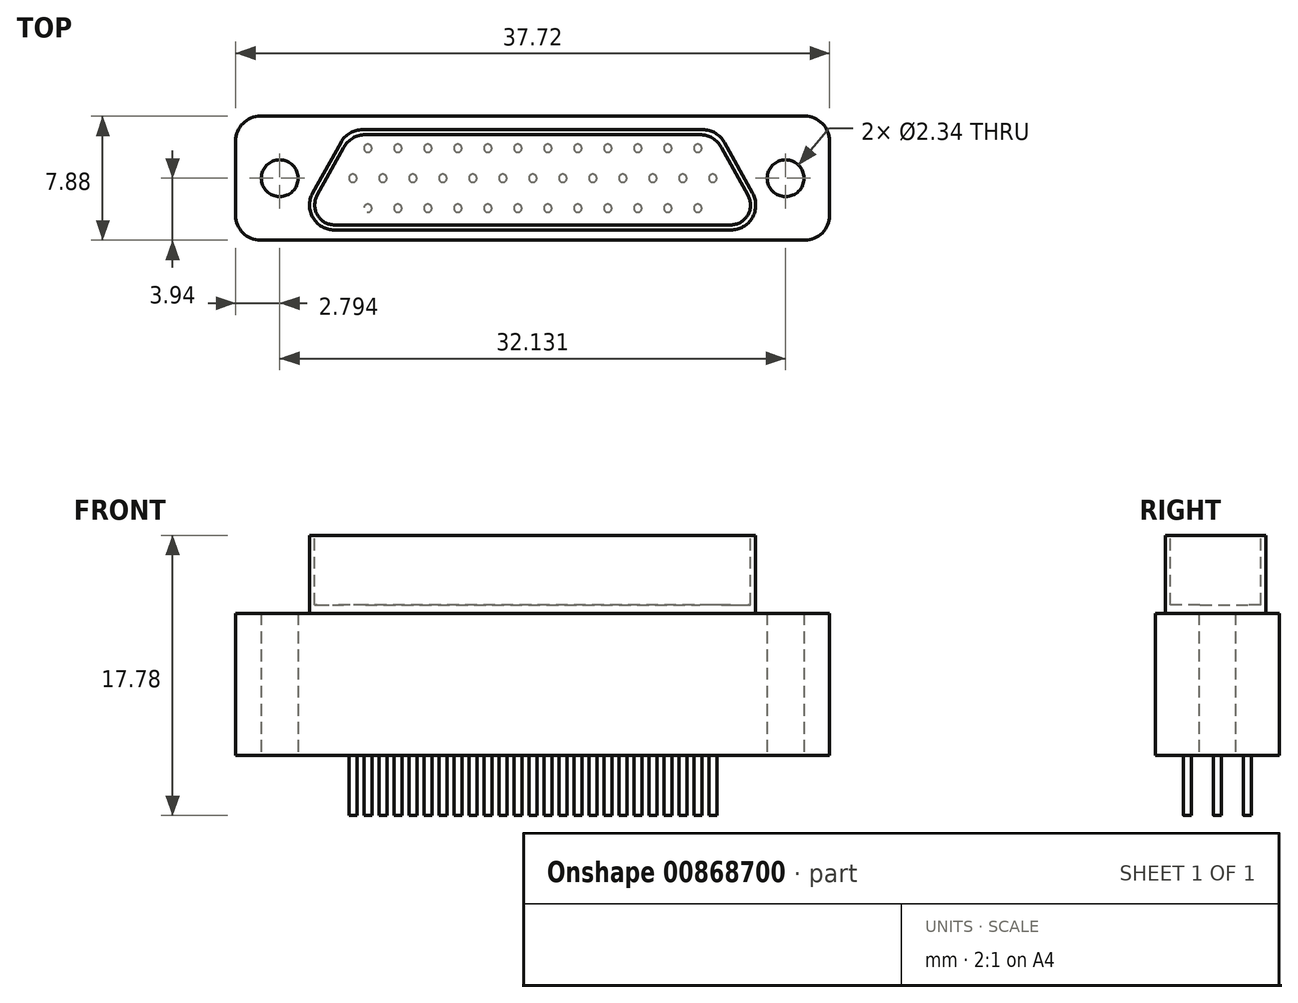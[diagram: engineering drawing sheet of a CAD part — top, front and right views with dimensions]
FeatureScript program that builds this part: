
annotation { "Feature Type Name" : "Feature", "Feature Type Description" : "" }
export const myFeature = defineFeature(function(context is Context, id is Id, definition is map)
    precondition{}
    {
        {
            var Q0;
            Q0=qCreatedBy(makeId("Top.planeOp"),FACE);
            var sketch = newSketch(context, id + "F0", { "sketchPlane" : qUnion([Q0])});
            skLineSegment(sketch, "E0.bottom", {"start": v(-17.28, 3.94) * mm, "end": v(17.28, 3.94) * mm});
            skLineSegment(sketch, "E0.top", {"start": v(-17.28, -3.94) * mm, "end": v(17.28, -3.94) * mm});
            skLineSegment(sketch, "E0.left", {"start": v(-18.86, 2.36) * mm, "end": v(-18.86, -2.36) * mm});
            skLineSegment(sketch, "E0.right", {"start": v(18.86, 2.36) * mm, "end": v(18.86, -2.36) * mm});
            skPoint(sketch, "E0.middle", {"position": v(0, 0) * mm});
            skCircle(sketch, "E1", {"center": v(-16.07, 0) * mm, "radius": 1.17 * mm});
            skCircle(sketch, "E2", {"center": v(16.07, 0) * mm, "radius": 1.17 * mm});
            skPoint(sketch, "E3.visualSharp", {"position": v(-18.86, -3.94) * mm});
            skArc(sketch, "E3.filletArc", {"start": v(-18.86, -2.36) * mm, "mid": v(-18.4, -3.48) * mm, "end": v(-17.28, -3.94) * mm});
            skPoint(sketch, "E4.visualSharp", {"position": v(-18.86, 3.94) * mm});
            skArc(sketch, "E4.filletArc", {"start": v(-17.28, 3.94) * mm, "mid": v(-18.4, 3.48) * mm, "end": v(-18.86, 2.36) * mm});
            skPoint(sketch, "E5.visualSharp", {"position": v(18.86, 3.94) * mm});
            skArc(sketch, "E5.filletArc", {"start": v(18.86, 2.36) * mm, "mid": v(18.4, 3.48) * mm, "end": v(17.28, 3.94) * mm});
            skPoint(sketch, "E6.visualSharp", {"position": v(18.86, -3.94) * mm});
            skArc(sketch, "E6.filletArc", {"start": v(17.28, -3.94) * mm, "mid": v(18.4, -3.48) * mm, "end": v(18.86, -2.36) * mm});
            skSolve(sketch);
        }
        {
            var Q0;
            Q0=makeQuery(id+"F0.imprint","IMPRINT",FACE,{"disambiguationData":[TD([[makeQuery(id+"F0.imprint","IMPRINT",EDGE,{"derivedFrom":sQuery(id+"F0.wireOp",EDGE,"E0.bottom")}),-1.0]])]});
            extrude(context, id + "F1", {"entities" : qUnion([Q0]), "endBound" : BoundingType.SYMMETRIC, "depth" : 9.02 * mm, "offsetDistance" : 25.4 * mm});
        }
        {
            var Q0;
            Q0=makeQuery(id+"F1.opExtrude","CAP_FACE",FACE,{"disambiguationData":[OSD([sQuery(id+"F0.wireOp",EDGE,"E0.bottom"),sQuery(id+"F0.wireOp",EDGE,"E0.top"),sQuery(id+"F0.wireOp",EDGE,"E0.left"),sQuery(id+"F0.wireOp",EDGE,"E0.right"),sQuery(id+"F0.wireOp",EDGE,"E1"),sQuery(id+"F0.wireOp",EDGE,"E2"),sQuery(id+"F0.wireOp",EDGE,"E3.filletArc"),sQuery(id+"F0.wireOp",EDGE,"E4.filletArc"),sQuery(id+"F0.wireOp",EDGE,"E5.filletArc"),sQuery(id+"F0.wireOp",EDGE,"E6.filletArc")])],"isStart":false});
            var sketch = newSketch(context, id + "F2", { "sketchPlane" : qUnion([Q0])});
            skPoint(sketch, "E7.middle", {"position": v(0, 0) * mm});
            skLineSegment(sketch, "E8.top", {"start": v(12.6, -3.29) * mm, "end": v(-12.6, -3.29) * mm});
            skLineSegment(sketch, "E9", {"start": v(-10.8, 3.09) * mm, "end": v(10.8, 3.09) * mm});
            skLineSegment(sketch, "E10", {"start": v(-13.97, -0.95) * mm, "end": v(-12.18, 2.27) * mm});
            skLineSegment(sketch, "E11", {"start": v(12.18, 2.27) * mm, "end": v(13.97, -0.95) * mm});
            skPoint(sketch, "E12.visualSharp", {"position": v(-11.73, 3.09) * mm});
            skArc(sketch, "E12.filletArc", {"start": v(-10.8, 3.09) * mm, "mid": v(-11.6, 2.87) * mm, "end": v(-12.18, 2.27) * mm});
            skPoint(sketch, "E13.visualSharp", {"position": v(-15.27, -3.29) * mm});
            skArc(sketch, "E13.filletArc", {"start": v(-13.97, -0.95) * mm, "mid": v(-13.95, -2.51) * mm, "end": v(-12.6, -3.29) * mm});
            skPoint(sketch, "E14.visualSharp", {"position": v(15.27, -3.29) * mm});
            skArc(sketch, "E14.filletArc", {"start": v(12.6, -3.29) * mm, "mid": v(13.95, -2.51) * mm, "end": v(13.97, -0.95) * mm});
            skPoint(sketch, "E15.visualSharp", {"position": v(11.73, 3.09) * mm});
            skArc(sketch, "E15.filletArc", {"start": v(12.18, 2.27) * mm, "mid": v(11.6, 2.87) * mm, "end": v(10.8, 3.09) * mm});
            skSolve(sketch);
        }
        {
            var Q0;
            Q0=qSketchRegion(id+"F2",true);
            extrude(context, id + "F3", {"entities" : qUnion([Q0]), "operationType" : NewBodyOperationType.ADD, "depth" : 4.95 * mm, "offsetDistance" : 25.4 * mm});
        }
        {
            var Q0;
            Q0=makeQuery(id+"F3.opExtrude","CAP_FACE",FACE,{"disambiguationData":[OSD([sQuery(id+"F2.wireOp",EDGE,"E8.top"),sQuery(id+"F2.wireOp",EDGE,"E9"),sQuery(id+"F2.wireOp",EDGE,"E10"),sQuery(id+"F2.wireOp",EDGE,"E11"),sQuery(id+"F2.wireOp",EDGE,"E12.filletArc"),sQuery(id+"F2.wireOp",EDGE,"E13.filletArc"),sQuery(id+"F2.wireOp",EDGE,"E14.filletArc"),sQuery(id+"F2.wireOp",EDGE,"E15.filletArc")])],"isStart":false});
            var sketch = newSketch(context, id + "F4", { "sketchPlane" : qUnion([Q0])});
            skLineSegment(sketch, "E16", {"start": v(-10.62, 2.77) * mm, "end": v(10.62, 2.77) * mm});
            skLineSegment(sketch, "E17", {"start": v(12, 1.96) * mm, "end": v(13.68, -1.09) * mm});
            skLineSegment(sketch, "E18", {"start": v(12.57, -2.97) * mm, "end": v(-12.57, -2.97) * mm});
            skLineSegment(sketch, "E19", {"start": v(-13.68, -1.09) * mm, "end": v(-12, 1.96) * mm});
            skPoint(sketch, "E20.visualSharp", {"position": v(-14.73, -2.97) * mm});
            skArc(sketch, "E20.filletArc", {"start": v(-13.68, -1.09) * mm, "mid": v(-13.66, -2.35) * mm, "end": v(-12.57, -2.97) * mm});
            skPoint(sketch, "E21.visualSharp", {"position": v(-11.54, 2.77) * mm});
            skArc(sketch, "E21.filletArc", {"start": v(-10.62, 2.77) * mm, "mid": v(-11.42, 2.55) * mm, "end": v(-12, 1.96) * mm});
            skPoint(sketch, "E22.visualSharp", {"position": v(11.55, 2.77) * mm});
            skArc(sketch, "E22.filletArc", {"start": v(12, 1.96) * mm, "mid": v(11.42, 2.55) * mm, "end": v(10.62, 2.77) * mm});
            skPoint(sketch, "E23.visualSharp", {"position": v(14.73, -2.97) * mm});
            skArc(sketch, "E23.filletArc", {"start": v(12.57, -2.97) * mm, "mid": v(13.67, -2.35) * mm, "end": v(13.68, -1.09) * mm});
            skSolve(sketch);
        }
        {
            var Q0;
            Q0=qSketchRegion(id+"F4",true);
            extrude(context, id + "F5", {"entities" : qUnion([Q0]), "operationType" : NewBodyOperationType.REMOVE, "depth" : -4.4 * mm, "offsetDistance" : 25.4 * mm});
        }
        {
            var Q0;
            Q0=makeQuery(id+"F1.opExtrude","CAP_FACE",FACE,{"disambiguationData":[OSD([sQuery(id+"F0.wireOp",EDGE,"E0.bottom"),sQuery(id+"F0.wireOp",EDGE,"E0.top"),sQuery(id+"F0.wireOp",EDGE,"E0.left"),sQuery(id+"F0.wireOp",EDGE,"E0.right"),sQuery(id+"F0.wireOp",EDGE,"E1"),sQuery(id+"F0.wireOp",EDGE,"E2"),sQuery(id+"F0.wireOp",EDGE,"E3.filletArc"),sQuery(id+"F0.wireOp",EDGE,"E4.filletArc"),sQuery(id+"F0.wireOp",EDGE,"E5.filletArc"),sQuery(id+"F0.wireOp",EDGE,"E6.filletArc")])],"isStart":true});
            var sketch = newSketch(context, id + "F6", { "sketchPlane" : qUnion([Q0])});
            skCircle(sketch, "E24", {"center": v(-10.46, 1.9) * mm, "radius": 0.25 * mm});
            skCircle(sketch, "E25.1.0.0", {"center": v(-8.56, 1.9) * mm, "radius": 0.25 * mm});
            skCircle(sketch, "E25.2.0.0", {"center": v(-6.65, 1.9) * mm, "radius": 0.25 * mm});
            skCircle(sketch, "E25.3.0.0", {"center": v(-4.75, 1.9) * mm, "radius": 0.25 * mm});
            skCircle(sketch, "E25.4.0.0", {"center": v(-2.84, 1.9) * mm, "radius": 0.25 * mm});
            skCircle(sketch, "E25.5.0.0", {"center": v(-0.94, 1.9) * mm, "radius": 0.25 * mm});
            skCircle(sketch, "E25.6.0.0", {"center": v(0.97, 1.9) * mm, "radius": 0.25 * mm});
            skCircle(sketch, "E25.7.0.0", {"center": v(2.87, 1.9) * mm, "radius": 0.25 * mm});
            skCircle(sketch, "E25.8.0.0", {"center": v(4.78, 1.9) * mm, "radius": 0.25 * mm});
            skCircle(sketch, "E25.9.0.0", {"center": v(6.68, 1.9) * mm, "radius": 0.25 * mm});
            skCircle(sketch, "E25.10.0.0", {"center": v(8.59, 1.9) * mm, "radius": 0.25 * mm});
            skCircle(sketch, "E25.11.0.0", {"center": v(10.5, 1.9) * mm, "radius": 0.25 * mm});
            skLineSegment(sketch, "E25.direction1", {"start": v(-10.46, 1.9) * mm, "end": v(-8.56, 1.9) * mm, "construction": true});
            skCircle(sketch, "E26", {"center": v(-11.42, 0) * mm, "radius": 0.25 * mm});
            skCircle(sketch, "E27.1.0.0", {"center": v(-9.51, 0) * mm, "radius": 0.25 * mm});
            skCircle(sketch, "E27.2.0.0", {"center": v(-7.6, 0) * mm, "radius": 0.25 * mm});
            skCircle(sketch, "E27.3.0.0", {"center": v(-5.7, 0) * mm, "radius": 0.25 * mm});
            skCircle(sketch, "E27.4.0.0", {"center": v(-3.8, 0) * mm, "radius": 0.25 * mm});
            skCircle(sketch, "E27.5.0.0", {"center": v(-1.9, 0) * mm, "radius": 0.25 * mm});
            skLineSegment(sketch, "E27.direction1", {"start": v(-11.42, 0) * mm, "end": v(-9.51, 0) * mm, "construction": true});
            skCircle(sketch, "E28", {"center": v(-10.46, -1.9) * mm, "radius": 0.25 * mm});
            skCircle(sketch, "E29.1.0.0", {"center": v(-8.56, -1.9) * mm, "radius": 0.25 * mm});
            skCircle(sketch, "E29.2.0.0", {"center": v(-6.65, -1.9) * mm, "radius": 0.25 * mm});
            skCircle(sketch, "E29.3.0.0", {"center": v(-4.75, -1.9) * mm, "radius": 0.25 * mm});
            skCircle(sketch, "E29.4.0.0", {"center": v(-2.84, -1.9) * mm, "radius": 0.25 * mm});
            skCircle(sketch, "E29.5.0.0", {"center": v(-0.94, -1.9) * mm, "radius": 0.25 * mm});
            skLineSegment(sketch, "E29.direction1", {"start": v(-10.46, -1.9) * mm, "end": v(-8.56, -1.9) * mm, "construction": true});
            skCircle(sketch, "E30.0.6.0", {"center": v(0.01, 0) * mm, "radius": 0.25 * mm});
            skCircle(sketch, "E30.0.7.0", {"center": v(1.92, 0) * mm, "radius": 0.25 * mm});
            skCircle(sketch, "E30.0.8.0", {"center": v(3.82, 0) * mm, "radius": 0.25 * mm});
            skCircle(sketch, "E30.0.9.0", {"center": v(5.73, 0) * mm, "radius": 0.25 * mm});
            skCircle(sketch, "E30.0.10.0", {"center": v(7.63, 0) * mm, "radius": 0.25 * mm});
            skCircle(sketch, "E30.0.11.0", {"center": v(9.54, 0) * mm, "radius": 0.25 * mm});
            skCircle(sketch, "E30.0.12.0", {"center": v(11.44, 0) * mm, "radius": 0.25 * mm});
            skCircle(sketch, "E31.0.6.0", {"center": v(0.97, -1.9) * mm, "radius": 0.25 * mm});
            skCircle(sketch, "E31.0.7.0", {"center": v(2.87, -1.9) * mm, "radius": 0.25 * mm});
            skCircle(sketch, "E31.0.8.0", {"center": v(4.78, -1.9) * mm, "radius": 0.25 * mm});
            skCircle(sketch, "E31.0.9.0", {"center": v(6.68, -1.9) * mm, "radius": 0.25 * mm});
            skCircle(sketch, "E31.0.10.0", {"center": v(8.59, -1.9) * mm, "radius": 0.25 * mm});
            skCircle(sketch, "E31.0.11.0", {"center": v(10.5, -1.9) * mm, "radius": 0.25 * mm});
            skSolve(sketch);
        }
        {
            var Q0;
            Q0=qSketchRegion(id+"F6",true);
            extrude(context, id + "F7", {"entities" : qUnion([Q0]), "operationType" : NewBodyOperationType.ADD, "depth" : 3.8 * mm, "offsetDistance" : 25.4 * mm});
        }
    });
